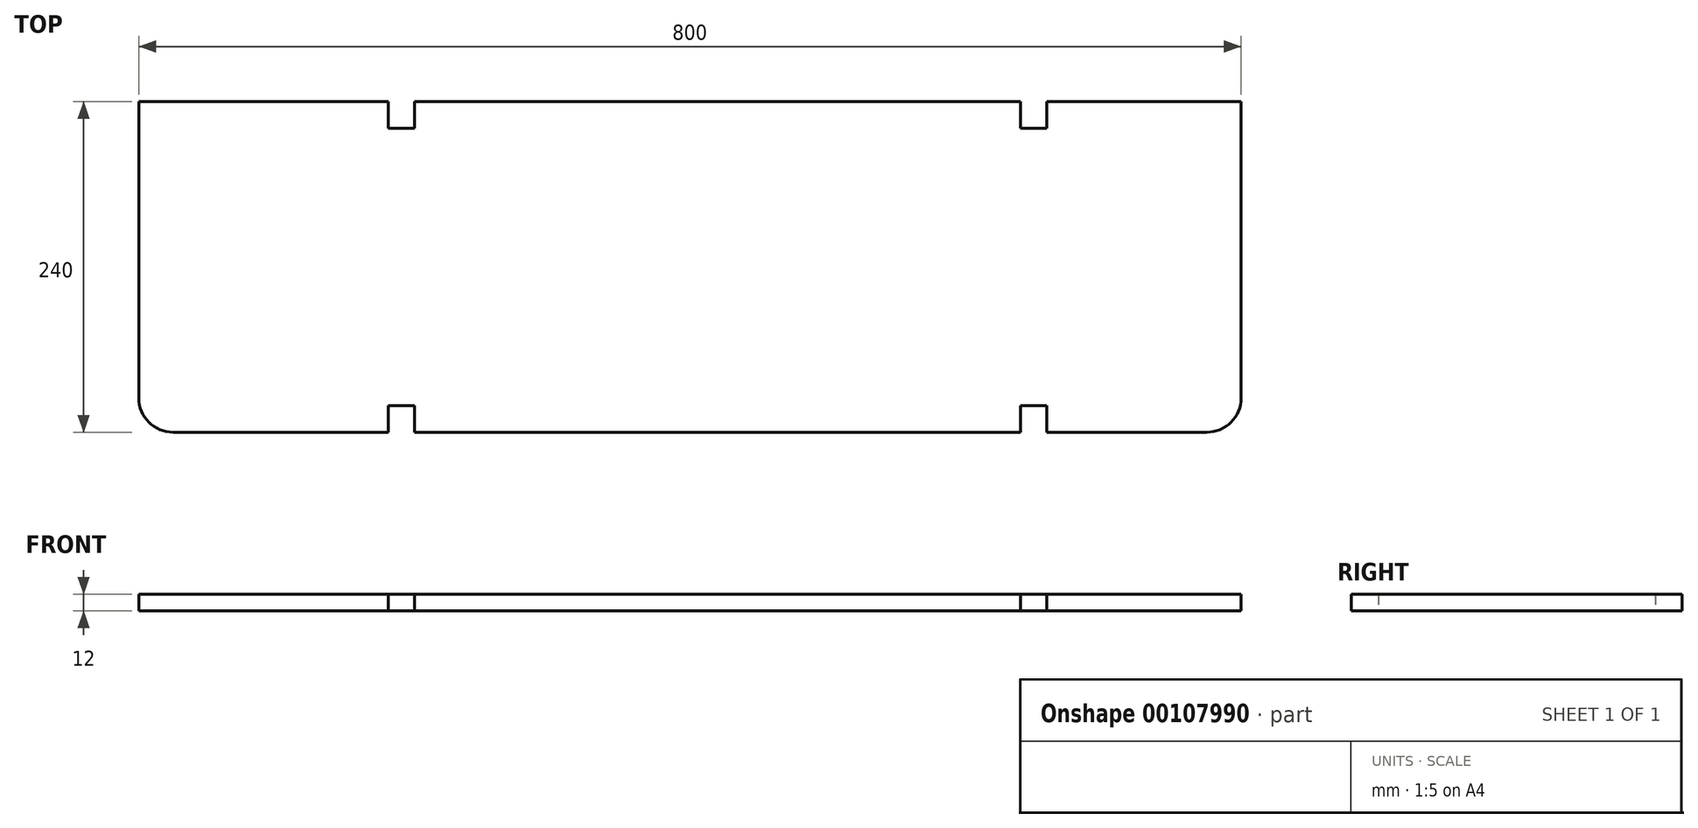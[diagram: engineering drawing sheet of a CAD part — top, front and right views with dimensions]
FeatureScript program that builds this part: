
annotation { "Feature Type Name" : "Feature", "Feature Type Description" : "" }
export const myFeature = defineFeature(function(context is Context, id is Id, definition is map)
    precondition{}
    {
        {
            var Q0;
            Q0=qCreatedBy(makeId("Top.planeOp"),FACE);
            var sketch = newSketch(context, id + "F0", { "sketchPlane" : qUnion([Q0])});
            skLineSegment(sketch, "E0.bottom", {"start": v(-392.99, 166.03) * mm, "end": v(-211.99, 166.03) * mm});
            skLineSegment(sketch, "E0.top", {"start": v(-367.99, -73.97) * mm, "end": v(-211.99, -73.97) * mm});
            skLineSegment(sketch, "E0.left", {"start": v(-392.99, 166.03) * mm, "end": v(-392.99, -48.97) * mm});
            skLineSegment(sketch, "E0.right", {"start": v(407.01, 166.03) * mm, "end": v(407.01, -48.97) * mm});
            skLineSegment(sketch, "E1.top", {"start": v(-211.99, 146.53) * mm, "end": v(-192.99, 146.53) * mm});
            skLineSegment(sketch, "E1.left", {"start": v(-211.99, 166.03) * mm, "end": v(-211.99, 146.53) * mm});
            skLineSegment(sketch, "E1.right", {"start": v(-192.99, 166.03) * mm, "end": v(-192.99, 146.53) * mm});
            skLineSegment(sketch, "E2.bottom", {"start": v(-211.99, -54.47) * mm, "end": v(-192.99, -54.47) * mm});
            skLineSegment(sketch, "E2.left", {"start": v(-211.99, -54.47) * mm, "end": v(-211.99, -73.97) * mm});
            skLineSegment(sketch, "E2.right", {"start": v(-192.99, -54.47) * mm, "end": v(-192.99, -73.97) * mm});
            skLineSegment(sketch, "E3.top", {"start": v(247.01, 146.53) * mm, "end": v(266.01, 146.53) * mm});
            skLineSegment(sketch, "E3.left", {"start": v(247.01, 166.03) * mm, "end": v(247.01, 146.53) * mm});
            skLineSegment(sketch, "E3.right", {"start": v(266.01, 166.03) * mm, "end": v(266.01, 146.53) * mm});
            skLineSegment(sketch, "E4.bottom", {"start": v(247.01, -54.47) * mm, "end": v(266.01, -54.47) * mm});
            skLineSegment(sketch, "E4.left", {"start": v(247.01, -54.47) * mm, "end": v(247.01, -73.97) * mm});
            skLineSegment(sketch, "E4.right", {"start": v(266.01, -54.47) * mm, "end": v(266.01, -73.97) * mm});
            skLineSegment(sketch, "E5.trimOffspring", {"start": v(-192.99, -73.97) * mm, "end": v(247.01, -73.97) * mm});
            skLineSegment(sketch, "E6.trimOffspring", {"start": v(266.01, -73.97) * mm, "end": v(382.01, -73.97) * mm});
            skLineSegment(sketch, "E7.trimOffspring", {"start": v(-192.99, 166.03) * mm, "end": v(247.01, 166.03) * mm});
            skLineSegment(sketch, "E8.trimOffspring", {"start": v(266.01, 166.03) * mm, "end": v(407.01, 166.03) * mm});
            skPoint(sketch, "E9.visualSharp", {"position": v(407.01, -73.97) * mm});
            skArc(sketch, "E9.filletArc", {"start": v(382.01, -73.97) * mm, "mid": v(399.7, -66.65) * mm, "end": v(407.01, -48.97) * mm});
            skPoint(sketch, "E10.visualSharp", {"position": v(-392.99, -73.97) * mm});
            skArc(sketch, "E10.filletArc", {"start": v(-392.99, -48.97) * mm, "mid": v(-385.66, -66.65) * mm, "end": v(-367.99, -73.97) * mm});
            skSolve(sketch);
        }
        {
            var Q0;
            Q0 = qSketchRegion(id + "F0", true);
            extrude(context, id + "F1", {"entities" : qUnion([Q0]), "endBound" : BoundingType.SYMMETRIC, "depth" : 12 * mm});
        }
    });
